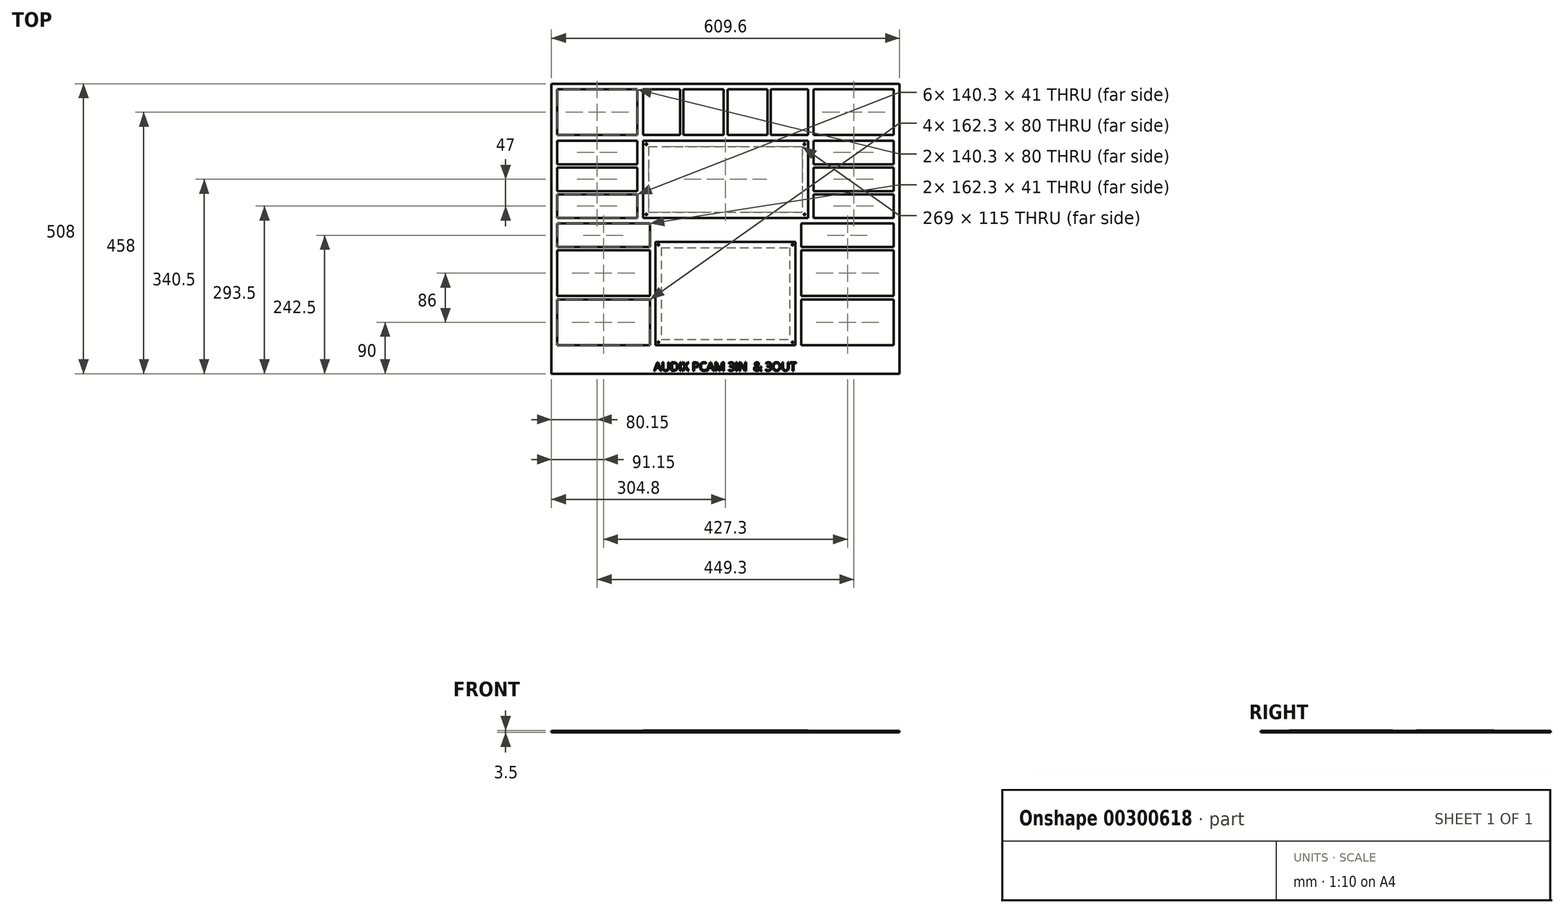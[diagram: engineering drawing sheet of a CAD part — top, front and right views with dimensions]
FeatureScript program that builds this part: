
annotation { "Feature Type Name" : "Feature", "Feature Type Description" : "" }
export const myFeature = defineFeature(function(context is Context, id is Id, definition is map)
    precondition{}
    {
        {
            var Q0;
            Q0=qCreatedBy(makeId("Top.planeOp"),FACE);
            var sketch = newSketch(context, id + "F0", { "sketchPlane" : qUnion([Q0])});
            skLineSegment(sketch, "E0.bottom", {"start": v(-304.8, 254) * mm, "end": v(304.8, 254) * mm});
            skLineSegment(sketch, "E0.top", {"start": v(-304.8, -254) * mm, "end": v(304.8, -254) * mm});
            skLineSegment(sketch, "E0.left", {"start": v(-304.8, 254) * mm, "end": v(-304.8, -254) * mm});
            skLineSegment(sketch, "E0.right", {"start": v(304.8, 254) * mm, "end": v(304.8, -254) * mm});
            skLineSegment(sketch, "E1", {"start": v(0, 0) * mm, "end": v(0, -254) * mm, "construction": true});
            skLineSegment(sketch, "E2", {"start": v(0, 0) * mm, "end": v(304.8, 0) * mm, "construction": true});
            skLineSegment(sketch, "E3.bottom", {"start": v(-144.5, 154) * mm, "end": v(144.5, 154) * mm});
            skLineSegment(sketch, "E3.top", {"start": v(-144.5, 19) * mm, "end": v(144.5, 19) * mm});
            skLineSegment(sketch, "E3.left", {"start": v(-144.5, 154) * mm, "end": v(-144.5, 19) * mm});
            skLineSegment(sketch, "E3.right", {"start": v(144.5, 154) * mm, "end": v(144.5, 19) * mm});
            skLineSegment(sketch, "E4", {"start": v(-304.8, 86.5) * mm, "end": v(304.8, 86.5) * mm, "construction": true});
            skPoint(sketch, "E4.startSnap0", {"position": v(-144.5, 86.5) * mm});
            skPoint(sketch, "E4.endSnap0", {"position": v(144.5, 86.5) * mm});
            skLineSegment(sketch, "E5", {"start": v(0, 154) * mm, "end": v(0, 254) * mm, "construction": true});
            skLineSegment(sketch, "E6.0", {"start": v(-134.5, 144) * mm, "end": v(134.5, 144) * mm});
            skLineSegment(sketch, "E6.1", {"start": v(-134.5, 144) * mm, "end": v(-134.5, 29) * mm});
            skLineSegment(sketch, "E6.2", {"start": v(-134.5, 29) * mm, "end": v(134.5, 29) * mm});
            skLineSegment(sketch, "E6.3", {"start": v(134.5, 144) * mm, "end": v(134.5, 29) * mm});
            skLineSegment(sketch, "E7.0", {"start": v(-138.5, 148) * mm, "end": v(138.5, 148) * mm, "construction": true});
            skLineSegment(sketch, "E7.1", {"start": v(-138.5, 148) * mm, "end": v(-138.5, 25) * mm, "construction": true});
            skLineSegment(sketch, "E7.2", {"start": v(-138.5, 25) * mm, "end": v(138.5, 25) * mm, "construction": true});
            skLineSegment(sketch, "E8.0", {"start": v(138.5, 148) * mm, "end": v(138.5, 25) * mm, "construction": true});
            skCircle(sketch, "E9", {"center": v(138.5, 148) * mm, "radius": 1.4 * mm});
            skCircle(sketch, "E10", {"center": v(138.5, 25) * mm, "radius": 1.4 * mm});
            skCircle(sketch, "E11", {"center": v(-138.5, 25) * mm, "radius": 1.4 * mm});
            skCircle(sketch, "E12", {"center": v(-138.5, 148) * mm, "radius": 1.4 * mm});
            skLineSegment(sketch, "E13.bottom", {"start": v(-294.8, 244) * mm, "end": v(-154.5, 244) * mm});
            skLineSegment(sketch, "E13.top", {"start": v(-294.8, 164) * mm, "end": v(-154.5, 164) * mm});
            skLineSegment(sketch, "E13.left", {"start": v(-294.8, 244) * mm, "end": v(-294.8, 164) * mm});
            skLineSegment(sketch, "E13.right", {"start": v(-154.5, 244) * mm, "end": v(-154.5, 164) * mm});
            skLineSegment(sketch, "E14.bottom", {"start": v(-294.8, 154) * mm, "end": v(-154.5, 154) * mm});
            skLineSegment(sketch, "E14.top", {"start": v(-294.8, 113) * mm, "end": v(-154.5, 113) * mm});
            skLineSegment(sketch, "E14.left", {"start": v(-294.8, 154) * mm, "end": v(-294.8, 113) * mm});
            skLineSegment(sketch, "E14.right", {"start": v(-154.5, 154) * mm, "end": v(-154.5, 113) * mm});
            skLineSegment(sketch, "E15.bottom", {"start": v(-294.8, 107) * mm, "end": v(-154.5, 107) * mm});
            skLineSegment(sketch, "E15.top", {"start": v(-294.8, 66) * mm, "end": v(-154.5, 66) * mm});
            skLineSegment(sketch, "E15.left", {"start": v(-294.8, 107) * mm, "end": v(-294.8, 66) * mm});
            skLineSegment(sketch, "E15.right", {"start": v(-154.5, 107) * mm, "end": v(-154.5, 66) * mm});
            skLineSegment(sketch, "E16.bottom", {"start": v(-294.8, 60) * mm, "end": v(-154.5, 60) * mm});
            skLineSegment(sketch, "E16.top", {"start": v(-294.8, 19) * mm, "end": v(-154.5, 19) * mm});
            skLineSegment(sketch, "E16.left", {"start": v(-294.8, 60) * mm, "end": v(-294.8, 19) * mm});
            skLineSegment(sketch, "E16.right", {"start": v(-154.5, 60) * mm, "end": v(-154.5, 19) * mm});
            skLineSegment(sketch, "E17.bottom", {"start": v(-144.5, 164) * mm, "end": v(-79.5, 164) * mm});
            skLineSegment(sketch, "E17.top", {"start": v(-144.5, 244) * mm, "end": v(-79.5, 244) * mm});
            skLineSegment(sketch, "E17.left", {"start": v(-144.5, 164) * mm, "end": v(-144.5, 244) * mm});
            skLineSegment(sketch, "E17.right", {"start": v(-79.5, 164) * mm, "end": v(-79.5, 244) * mm});
            skLineSegment(sketch, "E18.bottom", {"start": v(-73.5, 164) * mm, "end": v(-3.5, 164) * mm});
            skLineSegment(sketch, "E18.top", {"start": v(-73.5, 244) * mm, "end": v(-3.5, 244) * mm});
            skLineSegment(sketch, "E18.left", {"start": v(-73.5, 164) * mm, "end": v(-73.5, 244) * mm});
            skLineSegment(sketch, "E18.right", {"start": v(-3.5, 164) * mm, "end": v(-3.5, 244) * mm});
            skLineSegment(sketch, "E19.bottom", {"start": v(-294.8, 9) * mm, "end": v(-132.5, 9) * mm});
            skLineSegment(sketch, "E19.top", {"start": v(-294.8, -32) * mm, "end": v(-132.5, -32) * mm});
            skLineSegment(sketch, "E19.left", {"start": v(-294.8, 9) * mm, "end": v(-294.8, -32) * mm});
            skLineSegment(sketch, "E19.right", {"start": v(-132.5, 9) * mm, "end": v(-132.5, -32) * mm});
            skLineSegment(sketch, "E20.bottom", {"start": v(-122.5, -23) * mm, "end": v(122.5, -23) * mm});
            skLineSegment(sketch, "E20.top", {"start": v(-122.5, -204) * mm, "end": v(122.5, -204) * mm});
            skLineSegment(sketch, "E20.left", {"start": v(-122.5, -23) * mm, "end": v(-122.5, -204) * mm});
            skLineSegment(sketch, "E20.right", {"start": v(122.5, -23) * mm, "end": v(122.5, -204) * mm});
            skLineSegment(sketch, "E21", {"start": v(0, 0) * mm, "end": v(0, -204) * mm, "construction": true});
            skLineSegment(sketch, "E22", {"start": v(304.8, -113.5) * mm, "end": v(-304.8, -113.5) * mm, "construction": true});
            skPoint(sketch, "E22.startSnap0", {"position": v(122.5, -113.5) * mm});
            skPoint(sketch, "E22.endSnap0", {"position": v(-122.5, -113.5) * mm});
            skLineSegment(sketch, "E23.bottom", {"start": v(-294.8, -38) * mm, "end": v(-132.5, -38) * mm});
            skLineSegment(sketch, "E23.top", {"start": v(-294.8, -118) * mm, "end": v(-132.5, -118) * mm});
            skLineSegment(sketch, "E23.left", {"start": v(-294.8, -38) * mm, "end": v(-294.8, -118) * mm});
            skLineSegment(sketch, "E23.right", {"start": v(-132.5, -38) * mm, "end": v(-132.5, -118) * mm});
            skLineSegment(sketch, "E24.bottom", {"start": v(-294.8, -124) * mm, "end": v(-132.5, -124) * mm});
            skLineSegment(sketch, "E24.top", {"start": v(-294.8, -204) * mm, "end": v(-132.5, -204) * mm});
            skLineSegment(sketch, "E24.left", {"start": v(-294.8, -124) * mm, "end": v(-294.8, -204) * mm});
            skLineSegment(sketch, "E24.right", {"start": v(-132.5, -124) * mm, "end": v(-132.5, -204) * mm});
            skLineSegment(sketch, "E25.MirrorCS", {"start": v(294.8, 244) * mm, "end": v(154.5, 244) * mm});
            skLineSegment(sketch, "E26.MirrorCS", {"start": v(294.8, 244) * mm, "end": v(294.8, 164) * mm});
            skLineSegment(sketch, "E27.MirrorCS", {"start": v(294.8, 164) * mm, "end": v(154.5, 164) * mm});
            skLineSegment(sketch, "E28.MirrorCS", {"start": v(154.5, 244) * mm, "end": v(154.5, 164) * mm});
            skLineSegment(sketch, "E29.MirrorCS", {"start": v(144.5, 164) * mm, "end": v(144.5, 244) * mm});
            skLineSegment(sketch, "E30.MirrorCS", {"start": v(144.5, 244) * mm, "end": v(79.5, 244) * mm});
            skLineSegment(sketch, "E31.MirrorCS", {"start": v(144.5, 164) * mm, "end": v(79.5, 164) * mm});
            skLineSegment(sketch, "E32.MirrorCS", {"start": v(79.5, 164) * mm, "end": v(79.5, 244) * mm});
            skLineSegment(sketch, "E33.MirrorCS", {"start": v(73.5, 164) * mm, "end": v(3.5, 164) * mm});
            skLineSegment(sketch, "E34.MirrorCS", {"start": v(73.5, 164) * mm, "end": v(73.5, 244) * mm});
            skLineSegment(sketch, "E35.MirrorCS", {"start": v(3.5, 164) * mm, "end": v(3.5, 244) * mm});
            skLineSegment(sketch, "E36.MirrorCS", {"start": v(73.5, 244) * mm, "end": v(3.5, 244) * mm});
            skLineSegment(sketch, "E37.MirrorCS", {"start": v(294.8, 107) * mm, "end": v(294.8, 66) * mm});
            skLineSegment(sketch, "E38.MirrorCS", {"start": v(294.8, 66) * mm, "end": v(154.5, 66) * mm});
            skLineSegment(sketch, "E39.MirrorCS", {"start": v(154.5, 60) * mm, "end": v(154.5, 19) * mm});
            skLineSegment(sketch, "E40.MirrorCS", {"start": v(294.8, 113) * mm, "end": v(154.5, 113) * mm});
            skLineSegment(sketch, "E41.MirrorCS", {"start": v(294.8, 60) * mm, "end": v(154.5, 60) * mm});
            skLineSegment(sketch, "E42.MirrorCS", {"start": v(294.8, 107) * mm, "end": v(154.5, 107) * mm});
            skLineSegment(sketch, "E43.MirrorCS", {"start": v(294.8, 154) * mm, "end": v(154.5, 154) * mm});
            skLineSegment(sketch, "E44.MirrorCS", {"start": v(294.8, 154) * mm, "end": v(294.8, 113) * mm});
            skLineSegment(sketch, "E45.MirrorCS", {"start": v(294.8, 60) * mm, "end": v(294.8, 19) * mm});
            skLineSegment(sketch, "E46.MirrorCS", {"start": v(154.5, 154) * mm, "end": v(154.5, 113) * mm});
            skLineSegment(sketch, "E47.MirrorCS", {"start": v(154.5, 107) * mm, "end": v(154.5, 66) * mm});
            skLineSegment(sketch, "E48.MirrorCS", {"start": v(294.8, 19) * mm, "end": v(154.5, 19) * mm});
            skLineSegment(sketch, "E49.MirrorCS", {"start": v(294.8, 9) * mm, "end": v(294.8, -32) * mm});
            skLineSegment(sketch, "E50.MirrorCS", {"start": v(294.8, -32) * mm, "end": v(132.5, -32) * mm});
            skLineSegment(sketch, "E51.MirrorCS", {"start": v(294.8, -38) * mm, "end": v(132.5, -38) * mm});
            skLineSegment(sketch, "E52.MirrorCS", {"start": v(132.5, 9) * mm, "end": v(132.5, -32) * mm});
            skLineSegment(sketch, "E53.MirrorCS", {"start": v(132.5, -124) * mm, "end": v(132.5, -204) * mm});
            skLineSegment(sketch, "E54.MirrorCS", {"start": v(294.8, -118) * mm, "end": v(132.5, -118) * mm});
            skLineSegment(sketch, "E55.MirrorCS", {"start": v(132.5, -38) * mm, "end": v(132.5, -118) * mm});
            skLineSegment(sketch, "E56.MirrorCS", {"start": v(294.8, -124) * mm, "end": v(294.8, -204) * mm});
            skLineSegment(sketch, "E57.MirrorCS", {"start": v(294.8, -124) * mm, "end": v(132.5, -124) * mm});
            skLineSegment(sketch, "E58.MirrorCS", {"start": v(294.8, -204) * mm, "end": v(132.5, -204) * mm});
            skLineSegment(sketch, "E59.MirrorCS", {"start": v(294.8, -38) * mm, "end": v(294.8, -118) * mm});
            skLineSegment(sketch, "E60.MirrorCS", {"start": v(294.8, 9) * mm, "end": v(132.5, 9) * mm});
            skLineSegment(sketch, "E61.0", {"start": v(-112.5, -33) * mm, "end": v(112.5, -33) * mm});
            skLineSegment(sketch, "E61.1", {"start": v(-112.5, -33) * mm, "end": v(-112.5, -194) * mm});
            skLineSegment(sketch, "E61.2", {"start": v(-112.5, -194) * mm, "end": v(112.5, -194) * mm});
            skLineSegment(sketch, "E61.3", {"start": v(112.5, -33) * mm, "end": v(112.5, -194) * mm});
            skLineSegment(sketch, "E62.0", {"start": v(-117.5, -28) * mm, "end": v(117.5, -28) * mm, "construction": true});
            skLineSegment(sketch, "E62.1", {"start": v(-117.5, -28) * mm, "end": v(-117.5, -199) * mm, "construction": true});
            skLineSegment(sketch, "E62.2", {"start": v(-117.5, -199) * mm, "end": v(117.5, -199) * mm, "construction": true});
            skLineSegment(sketch, "E62.3", {"start": v(117.5, -28) * mm, "end": v(117.5, -199) * mm, "construction": true});
            skCircle(sketch, "E63", {"center": v(-117.5, -28) * mm, "radius": 1.4 * mm});
            skCircle(sketch, "E64", {"center": v(117.5, -28) * mm, "radius": 1.4 * mm});
            skCircle(sketch, "E65", {"center": v(117.5, -199) * mm, "radius": 1.4 * mm});
            skCircle(sketch, "E66", {"center": v(-117.5, -199) * mm, "radius": 1.4 * mm});
            skSolve(sketch);
        }
        {
            var Q0;
            Q0=makeQuery(id+"F0.imprint","IMPRINT",FACE,{"disambiguationData":[TD([[makeQuery(id+"F0.imprint","IMPRINT",EDGE,{"derivedFrom":sQuery(id+"F0.wireOp",EDGE,"E0.bottom")}),-1.0]])]});
            var Q1;
            Q1=makeQuery(id+"F0.imprint","IMPRINT",FACE,{"disambiguationData":[TD([[makeQuery(id+"F0.imprint","IMPRINT",EDGE,{"derivedFrom":sQuery(id+"F0.wireOp",EDGE,"E12")}),1.0]])]});
            var Q2;
            Q2=makeQuery(id+"F0.imprint","IMPRINT",FACE,{"disambiguationData":[TD([[makeQuery(id+"F0.imprint","IMPRINT",EDGE,{"derivedFrom":sQuery(id+"F0.wireOp",EDGE,"E9")}),1.0]])]});
            var Q3;
            Q3=makeQuery(id+"F0.imprint","IMPRINT",FACE,{"disambiguationData":[TD([[makeQuery(id+"F0.imprint","IMPRINT",EDGE,{"derivedFrom":sQuery(id+"F0.wireOp",EDGE,"E10")}),1.0]])]});
            var Q4;
            Q4=makeQuery(id+"F0.imprint","IMPRINT",FACE,{"disambiguationData":[TD([[makeQuery(id+"F0.imprint","IMPRINT",EDGE,{"derivedFrom":sQuery(id+"F0.wireOp",EDGE,"E11")}),1.0]])]});
            var Q5;
            Q5=makeQuery(id+"F0.imprint","IMPRINT",FACE,{"disambiguationData":[TD([[makeQuery(id+"F0.imprint","IMPRINT",EDGE,{"derivedFrom":sQuery(id+"F0.wireOp",EDGE,"E63")}),1.0]])]});
            var Q6;
            Q6=makeQuery(id+"F0.imprint","IMPRINT",FACE,{"disambiguationData":[TD([[makeQuery(id+"F0.imprint","IMPRINT",EDGE,{"derivedFrom":sQuery(id+"F0.wireOp",EDGE,"E64")}),1.0]])]});
            var Q7;
            Q7=makeQuery(id+"F0.imprint","IMPRINT",FACE,{"disambiguationData":[TD([[makeQuery(id+"F0.imprint","IMPRINT",EDGE,{"derivedFrom":sQuery(id+"F0.wireOp",EDGE,"E65")}),1.0]])]});
            var Q8;
            Q8=makeQuery(id+"F0.imprint","IMPRINT",FACE,{"disambiguationData":[TD([[makeQuery(id+"F0.imprint","IMPRINT",EDGE,{"derivedFrom":sQuery(id+"F0.wireOp",EDGE,"E66")}),1.0]])]});
            extrude(context, id + "F1", {"entities" : qUnion([Q0, Q1, Q2, Q3, Q4, Q5, Q6, Q7, Q8]), "depth" : 3 * mm});
        }
        {
            var Q0;
            Q0=makeQuery(id+"F0.imprint","IMPRINT",FACE,{"disambiguationData":[TD([[makeQuery(id+"F0.imprint","IMPRINT",EDGE,{"derivedFrom":sQuery(id+"F0.wireOp",EDGE,"E3.bottom")}),-1.0]])]});
            var Q1;
            Q1=makeQuery(id+"F0.imprint","IMPRINT",FACE,{"disambiguationData":[TD([[makeQuery(id+"F0.imprint","IMPRINT",EDGE,{"derivedFrom":sQuery(id+"F0.wireOp",EDGE,"E20.bottom")}),-1.0]])]});
            extrude(context, id + "F2", {"entities" : qUnion([Q0, Q1]), "operationType" : NewBodyOperationType.ADD, "depth" : 1.5 * mm});
        }
        {
            var Q0;
            Q0=makeQuery(id+"F1.opExtrude","CAP_FACE",FACE,{"disambiguationData":[OSD([sQuery(id+"F0.wireOp",EDGE,"E0.bottom"),sQuery(id+"F0.wireOp",EDGE,"E0.top"),sQuery(id+"F0.wireOp",EDGE,"E0.left"),sQuery(id+"F0.wireOp",EDGE,"E0.right"),sQuery(id+"F0.wireOp",EDGE,"E3.bottom"),sQuery(id+"F0.wireOp",EDGE,"E3.top"),sQuery(id+"F0.wireOp",EDGE,"E3.left"),sQuery(id+"F0.wireOp",EDGE,"E3.right"),sQuery(id+"F0.wireOp",EDGE,"E13.bottom"),sQuery(id+"F0.wireOp",EDGE,"E13.top"),sQuery(id+"F0.wireOp",EDGE,"E13.left"),sQuery(id+"F0.wireOp",EDGE,"E13.right"),sQuery(id+"F0.wireOp",EDGE,"E14.bottom"),sQuery(id+"F0.wireOp",EDGE,"E14.top"),sQuery(id+"F0.wireOp",EDGE,"E14.left"),sQuery(id+"F0.wireOp",EDGE,"E14.right"),sQuery(id+"F0.wireOp",EDGE,"E15.bottom"),sQuery(id+"F0.wireOp",EDGE,"E15.top"),sQuery(id+"F0.wireOp",EDGE,"E15.left"),sQuery(id+"F0.wireOp",EDGE,"E15.right"),sQuery(id+"F0.wireOp",EDGE,"E16.bottom"),sQuery(id+"F0.wireOp",EDGE,"E16.top"),sQuery(id+"F0.wireOp",EDGE,"E16.left"),sQuery(id+"F0.wireOp",EDGE,"E16.right"),sQuery(id+"F0.wireOp",EDGE,"E17.bottom"),sQuery(id+"F0.wireOp",EDGE,"E17.top"),sQuery(id+"F0.wireOp",EDGE,"E17.left"),sQuery(id+"F0.wireOp",EDGE,"E17.right"),sQuery(id+"F0.wireOp",EDGE,"E18.bottom"),sQuery(id+"F0.wireOp",EDGE,"E18.top"),sQuery(id+"F0.wireOp",EDGE,"E18.left"),sQuery(id+"F0.wireOp",EDGE,"E18.right"),sQuery(id+"F0.wireOp",EDGE,"E19.bottom"),sQuery(id+"F0.wireOp",EDGE,"E19.top"),sQuery(id+"F0.wireOp",EDGE,"E19.left"),sQuery(id+"F0.wireOp",EDGE,"E19.right"),sQuery(id+"F0.wireOp",EDGE,"E20.bottom"),sQuery(id+"F0.wireOp",EDGE,"E20.top"),sQuery(id+"F0.wireOp",EDGE,"E20.left"),sQuery(id+"F0.wireOp",EDGE,"E20.right"),sQuery(id+"F0.wireOp",EDGE,"E23.bottom"),sQuery(id+"F0.wireOp",EDGE,"E23.top"),sQuery(id+"F0.wireOp",EDGE,"E23.left"),sQuery(id+"F0.wireOp",EDGE,"E23.right"),sQuery(id+"F0.wireOp",EDGE,"E24.bottom"),sQuery(id+"F0.wireOp",EDGE,"E24.top"),sQuery(id+"F0.wireOp",EDGE,"E24.left"),sQuery(id+"F0.wireOp",EDGE,"E24.right"),sQuery(id+"F0.wireOp",EDGE,"E25.MirrorCS"),sQuery(id+"F0.wireOp",EDGE,"E26.MirrorCS"),sQuery(id+"F0.wireOp",EDGE,"E27.MirrorCS"),sQuery(id+"F0.wireOp",EDGE,"E28.MirrorCS"),sQuery(id+"F0.wireOp",EDGE,"E29.MirrorCS"),sQuery(id+"F0.wireOp",EDGE,"E30.MirrorCS"),sQuery(id+"F0.wireOp",EDGE,"E31.MirrorCS"),sQuery(id+"F0.wireOp",EDGE,"E32.MirrorCS"),sQuery(id+"F0.wireOp",EDGE,"E33.MirrorCS"),sQuery(id+"F0.wireOp",EDGE,"E34.MirrorCS"),sQuery(id+"F0.wireOp",EDGE,"E35.MirrorCS"),sQuery(id+"F0.wireOp",EDGE,"E36.MirrorCS"),sQuery(id+"F0.wireOp",EDGE,"E37.MirrorCS"),sQuery(id+"F0.wireOp",EDGE,"E38.MirrorCS"),sQuery(id+"F0.wireOp",EDGE,"E39.MirrorCS"),sQuery(id+"F0.wireOp",EDGE,"E40.MirrorCS"),sQuery(id+"F0.wireOp",EDGE,"E41.MirrorCS"),sQuery(id+"F0.wireOp",EDGE,"E42.MirrorCS"),sQuery(id+"F0.wireOp",EDGE,"E43.MirrorCS"),sQuery(id+"F0.wireOp",EDGE,"E44.MirrorCS"),sQuery(id+"F0.wireOp",EDGE,"E45.MirrorCS"),sQuery(id+"F0.wireOp",EDGE,"E46.MirrorCS"),sQuery(id+"F0.wireOp",EDGE,"E47.MirrorCS"),sQuery(id+"F0.wireOp",EDGE,"E48.MirrorCS"),sQuery(id+"F0.wireOp",EDGE,"E49.MirrorCS"),sQuery(id+"F0.wireOp",EDGE,"E50.MirrorCS"),sQuery(id+"F0.wireOp",EDGE,"E51.MirrorCS"),sQuery(id+"F0.wireOp",EDGE,"E52.MirrorCS"),sQuery(id+"F0.wireOp",EDGE,"E53.MirrorCS"),sQuery(id+"F0.wireOp",EDGE,"E54.MirrorCS"),sQuery(id+"F0.wireOp",EDGE,"E55.MirrorCS"),sQuery(id+"F0.wireOp",EDGE,"E56.MirrorCS"),sQuery(id+"F0.wireOp",EDGE,"E57.MirrorCS"),sQuery(id+"F0.wireOp",EDGE,"E58.MirrorCS"),sQuery(id+"F0.wireOp",EDGE,"E59.MirrorCS"),sQuery(id+"F0.wireOp",EDGE,"E60.MirrorCS")])],"isStart":false});
            var sketch = newSketch(context, id + "F3", { "sketchPlane" : qUnion([Q0])});
            skText(sketch, "E67", { "text": "AUDIX PCAM 3IN  & 3OUT", "fontName": "OpenSans-Regular.ttf"});
            skPoint(sketch, "E68", {"position": v(0, -204) * mm});
            const initialGuessF3  = {"E67": [-0.12537, -0.249, 1, 0, 0.015]};
            skSetInitialGuess(sketch, initialGuessF3);
            skSolve(sketch);
        }
        {
            var Q0;
            Q0=makeQuery(id+"F3.imprint","IMPRINT",FACE,{"disambiguationData":[TD([[makeQuery(id+"F3.imprint","IMPRINT",EDGE,{"derivedFrom":sQuery(id+"F3.wireOp",EDGE,"E67.sketch_text.stroke-0")}),-1.0]])]});
            var Q1;
            Q1=makeQuery(id+"F3.imprint","IMPRINT",FACE,{"disambiguationData":[TD([[makeQuery(id+"F3.imprint","IMPRINT",EDGE,{"derivedFrom":sQuery(id+"F3.wireOp",EDGE,"E67.sketch_text.stroke-13")}),-1.0]])]});
            var Q2;
            Q2=makeQuery(id+"F3.imprint","IMPRINT",FACE,{"disambiguationData":[TD([[makeQuery(id+"F3.imprint","IMPRINT",EDGE,{"derivedFrom":sQuery(id+"F3.wireOp",EDGE,"E67.sketch_text.stroke-27")}),-1.0]])]});
            var Q3;
            Q3=makeQuery(id+"F3.imprint","IMPRINT",FACE,{"disambiguationData":[TD([[makeQuery(id+"F3.imprint","IMPRINT",EDGE,{"derivedFrom":sQuery(id+"F3.wireOp",EDGE,"E67.sketch_text.stroke-41")}),-1.0]])]});
            var Q4;
            Q4=makeQuery(id+"F3.imprint","IMPRINT",FACE,{"disambiguationData":[TD([[makeQuery(id+"F3.imprint","IMPRINT",EDGE,{"derivedFrom":sQuery(id+"F3.wireOp",EDGE,"E67.sketch_text.stroke-45")}),-1.0]])]});
            var Q5;
            Q5=makeQuery(id+"F3.imprint","IMPRINT",FACE,{"disambiguationData":[TD([[makeQuery(id+"F3.imprint","IMPRINT",EDGE,{"derivedFrom":sQuery(id+"F3.wireOp",EDGE,"E67.sketch_text.stroke-57")}),-1.0]])]});
            var Q6;
            Q6=makeQuery(id+"F3.imprint","IMPRINT",FACE,{"disambiguationData":[TD([[makeQuery(id+"F3.imprint","IMPRINT",EDGE,{"derivedFrom":sQuery(id+"F3.wireOp",EDGE,"E67.sketch_text.stroke-72")}),-1.0]])]});
            var Q7;
            Q7=makeQuery(id+"F3.imprint","IMPRINT",FACE,{"disambiguationData":[TD([[makeQuery(id+"F3.imprint","IMPRINT",EDGE,{"derivedFrom":sQuery(id+"F3.wireOp",EDGE,"E67.sketch_text.stroke-87")}),-1.0]])]});
            var Q8;
            Q8=makeQuery(id+"F3.imprint","IMPRINT",FACE,{"disambiguationData":[TD([[makeQuery(id+"F3.imprint","IMPRINT",EDGE,{"derivedFrom":sQuery(id+"F3.wireOp",EDGE,"E67.sketch_text.stroke-100")}),-1.0]])]});
            var Q9;
            Q9=makeQuery(id+"F3.imprint","IMPRINT",FACE,{"disambiguationData":[TD([[makeQuery(id+"F3.imprint","IMPRINT",EDGE,{"derivedFrom":sQuery(id+"F3.wireOp",EDGE,"E67.sketch_text.stroke-118")}),-1.0]])]});
            var Q10;
            Q10=makeQuery(id+"F3.imprint","IMPRINT",FACE,{"disambiguationData":[TD([[makeQuery(id+"F3.imprint","IMPRINT",EDGE,{"derivedFrom":sQuery(id+"F3.wireOp",EDGE,"E67.sketch_text.stroke-146")}),-1.0]])]});
            var Q11;
            Q11=makeQuery(id+"F3.imprint","IMPRINT",FACE,{"disambiguationData":[TD([[makeQuery(id+"F3.imprint","IMPRINT",EDGE,{"derivedFrom":sQuery(id+"F3.wireOp",EDGE,"E67.sketch_text.stroke-150")}),-1.0]])]});
            var Q12;
            Q12=makeQuery(id+"F3.imprint","IMPRINT",FACE,{"disambiguationData":[TD([[makeQuery(id+"F3.imprint","IMPRINT",EDGE,{"derivedFrom":sQuery(id+"F3.wireOp",EDGE,"E67.sketch_text.stroke-165")}),-1.0]])]});
            var Q13;
            Q13=makeQuery(id+"F3.imprint","IMPRINT",FACE,{"disambiguationData":[TD([[makeQuery(id+"F3.imprint","IMPRINT",EDGE,{"derivedFrom":sQuery(id+"F3.wireOp",EDGE,"E67.sketch_text.stroke-203")}),-1.0]])]});
            var Q14;
            Q14=makeQuery(id+"F3.imprint","IMPRINT",FACE,{"disambiguationData":[TD([[makeQuery(id+"F3.imprint","IMPRINT",EDGE,{"derivedFrom":sQuery(id+"F3.wireOp",EDGE,"E67.sketch_text.stroke-231")}),-1.0]])]});
            var Q15;
            Q15=makeQuery(id+"F3.imprint","IMPRINT",FACE,{"disambiguationData":[TD([[makeQuery(id+"F3.imprint","IMPRINT",EDGE,{"derivedFrom":sQuery(id+"F3.wireOp",EDGE,"E67.sketch_text.stroke-247")}),-1.0]])]});
            var Q16;
            Q16=makeQuery(id+"F3.imprint","IMPRINT",FACE,{"disambiguationData":[TD([[makeQuery(id+"F3.imprint","IMPRINT",EDGE,{"derivedFrom":sQuery(id+"F3.wireOp",EDGE,"E67.sketch_text.stroke-261")}),-1.0]])]});
            extrude(context, id + "F4", {"entities" : qUnion([Q0, Q1, Q2, Q3, Q4, Q5, Q6, Q7, Q8, Q9, Q10, Q11, Q12, Q13, Q14, Q15, Q16]), "operationType" : NewBodyOperationType.REMOVE, "oppositeDirection" : true, "depth" : 2 * mm});
        }
        {
            var Q0;
            Q0=makeQuery(id+"F1.opExtrude","CAP_EDGE",EDGE,{"disambiguationData":[OSD([sQuery(id+"F0.wireOp",EDGE,"E12")])],"isStart":false});
            var Q1;
            Q1=makeQuery(id+"F1.opExtrude","CAP_EDGE",EDGE,{"disambiguationData":[OSD([sQuery(id+"F0.wireOp",EDGE,"E11")])],"isStart":false});
            var Q2;
            Q2=makeQuery(id+"F1.opExtrude","CAP_EDGE",EDGE,{"disambiguationData":[OSD([sQuery(id+"F0.wireOp",EDGE,"E10")])],"isStart":false});
            var Q3;
            Q3=makeQuery(id+"F1.opExtrude","CAP_EDGE",EDGE,{"disambiguationData":[OSD([sQuery(id+"F0.wireOp",EDGE,"E9")])],"isStart":false});
            var Q4;
            Q4=makeQuery(id+"F1.opExtrude","CAP_EDGE",EDGE,{"disambiguationData":[OSD([sQuery(id+"F0.wireOp",EDGE,"E64")])],"isStart":false});
            var Q5;
            Q5=makeQuery(id+"F1.opExtrude","CAP_EDGE",EDGE,{"disambiguationData":[OSD([sQuery(id+"F0.wireOp",EDGE,"E63")])],"isStart":false});
            var Q6;
            Q6=makeQuery(id+"F1.opExtrude","CAP_EDGE",EDGE,{"disambiguationData":[OSD([sQuery(id+"F0.wireOp",EDGE,"E66")])],"isStart":false});
            var Q7;
            Q7=makeQuery(id+"F1.opExtrude","CAP_EDGE",EDGE,{"disambiguationData":[OSD([sQuery(id+"F0.wireOp",EDGE,"E65")])],"isStart":false});
            chamfer(context, id + "F5", {"entities" : qUnion([Q0, Q1, Q2, Q3, Q4, Q5, Q6, Q7]), "chamferType" : ChamferType.OFFSET_ANGLE, "width" : .4 * mm, "oppositeDirection" : false, "angle" : 60 * degree, "tangentPropagation" : true});
        }
        {
            var Q0;
            Q0=makeQuery(id+"F0.imprint","IMPRINT",FACE,{"disambiguationData":[TD([[makeQuery(id+"F0.imprint","IMPRINT",EDGE,{"derivedFrom":sQuery(id+"F0.wireOp",EDGE,"E6.0")}),-1.0]])]});
            var Q1;
            Q1=makeQuery(id+"F0.imprint","IMPRINT",FACE,{"disambiguationData":[TD([[makeQuery(id+"F0.imprint","IMPRINT",EDGE,{"derivedFrom":sQuery(id+"F0.wireOp",EDGE,"E61.0")}),-1.0]])]});
            var Q2;
            Q2=makeQuery(id+"F0.imprint","IMPRINT",FACE,{"disambiguationData":[TD([[makeQuery(id+"F0.imprint","IMPRINT",EDGE,{"derivedFrom":sQuery(id+"F0.wireOp",EDGE,"E20.bottom")}),-1.0]])]});
            var Q3;
            Q3=makeQuery(id+"F0.imprint","IMPRINT",FACE,{"disambiguationData":[TD([[makeQuery(id+"F0.imprint","IMPRINT",EDGE,{"derivedFrom":sQuery(id+"F0.wireOp",EDGE,"E3.bottom")}),-1.0]])]});
            extrude(context, id + "F6", {"entities" : qUnion([Q0, Q1, Q2, Q3]), "depth" : 3.5 * mm, "hasSecondDirection" : true, "secondDirectionOppositeDirection" : false, "secondDirectionDepth" : 2 * mm});
        }
    });
